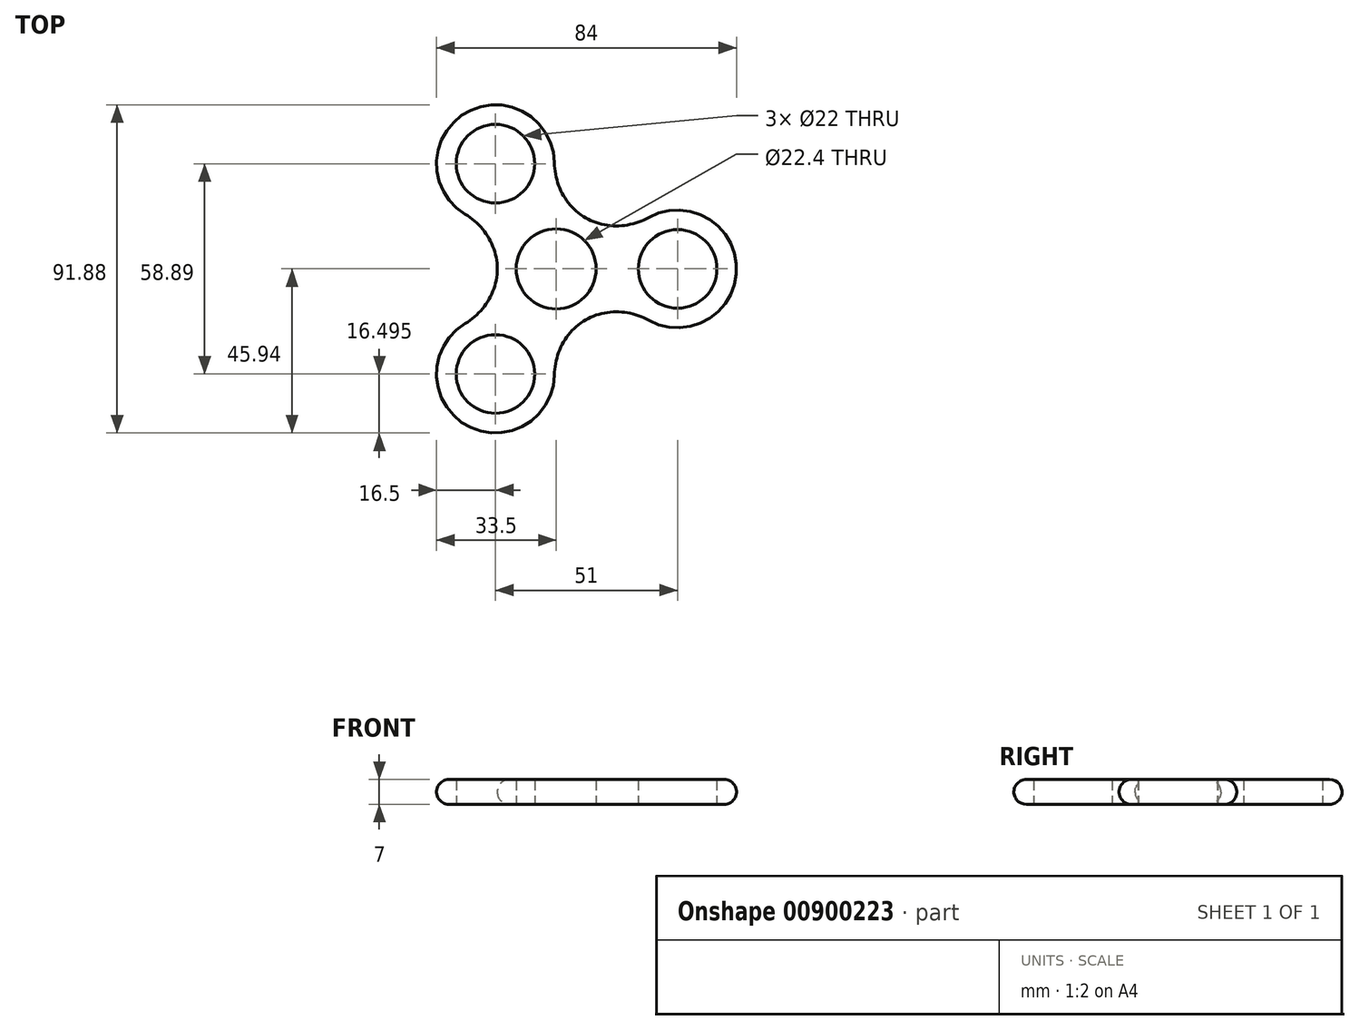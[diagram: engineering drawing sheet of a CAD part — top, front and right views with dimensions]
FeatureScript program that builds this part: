
annotation { "Feature Type Name" : "Feature", "Feature Type Description" : "" }
export const myFeature = defineFeature(function(context is Context, id is Id, definition is map)
    precondition{}
    {
        {
            assignVariable(context, id + "F0", {"name" : "thick", "anyValue" : 7});
        }
        {
            var Q0;
            Q0=qCreatedBy(makeId("Top.planeOp"),FACE);
            var sketch = newSketch(context, id + "F1", { "sketchPlane" : qUnion([Q0])});
            skCircle(sketch, "E0", {"center": v(0, 0) * mm, "radius": 11.2 * mm});
            skCircle(sketch, "E1", {"center": v(0, 0) * mm, "radius": 16.5 * mm});
            skCircle(sketch, "E2.1.0.0", {"center": v(34, 0) * mm, "radius": 16.5 * mm});
            skCircle(sketch, "E2.1.0.1", {"center": v(34, 0) * mm, "radius": 11 * mm});
            skLineSegment(sketch, "E2.direction2", {"start": v(0, 0) * mm, "end": v(0, 34) * mm, "construction": true});
            skCircle(sketch, "E3.1.0", {"center": v(-17, 29.44) * mm, "radius": 16.5 * mm});
            skCircle(sketch, "E3.1.1", {"center": v(-17, 29.44) * mm, "radius": 11 * mm});
            skCircle(sketch, "E3.2.0", {"center": v(-17, -29.44) * mm, "radius": 16.5 * mm});
            skCircle(sketch, "E3.2.1", {"center": v(-17, -29.44) * mm, "radius": 11 * mm});
            skLineSegment(sketch, "E4", {"start": v(0, 0) * mm, "end": v(-16.5, 0) * mm, "construction": true});
            skLineSegment(sketch, "E5.1.0", {"start": v(0, 0) * mm, "end": v(8.25, -14.29) * mm, "construction": true});
            skLineSegment(sketch, "E5.2.0", {"start": v(0, 0) * mm, "end": v(8.25, 14.29) * mm, "construction": true});
            skLineSegment(sketch, "E6", {"start": v(0, 0) * mm, "end": v(26, 14.43) * mm, "construction": true});
            skLineSegment(sketch, "E7.1.0", {"start": v(0, 0) * mm, "end": v(-25.5, 15.3) * mm, "construction": true});
            skLineSegment(sketch, "E7.2.0", {"start": v(0, 0) * mm, "end": v(-0.5, -29.72) * mm, "construction": true});
            skLineSegment(sketch, "E8", {"start": v(0, 0) * mm, "end": v(26, -14.43) * mm, "construction": true});
            skLineSegment(sketch, "E9.1.0", {"start": v(0, 0) * mm, "end": v(-0.5, 29.72) * mm, "construction": true});
            skLineSegment(sketch, "E9.2.0", {"start": v(0, 0) * mm, "end": v(-25.5, -15.3) * mm, "construction": true});
            skCircle(sketch, "E10", {"center": v(0, 0) * mm, "radius": 23 * mm, "construction": true});
            skFitSpline(sketch, "E11", {"points": [v(-0.5, 29.72) * mm, v(8.25, 14.29) * mm, v(26, 14.43) * mm], "startDerivative": vector(0.68, -40.36) * mm, "endDerivative": vector(35.3, 19.6) * mm});
            skFitSpline(sketch, "E12", {"points": [v(26, -14.43) * mm, v(8.25, -14.29) * mm, v(-0.5, -29.72) * mm], "startDerivative": vector(-35.3, 19.6) * mm, "endDerivative": vector(-0.68, -40.36) * mm});
            skFitSpline(sketch, "E13", {"points": [v(-25.5, -15.3) * mm, v(-16.5, 0) * mm, v(-25.5, 15.3) * mm], "startDerivative": vector(34.61, 20.77) * mm, "endDerivative": vector(-34.61, 20.77) * mm});
            skSolve(sketch);
        }
        {
            var Q0;
            Q0=makeQuery(id+"F1.imprint","IMPRINT",FACE,{"disambiguationData":[TD([[makeQuery(id+"F1.imprint","IMPRINT",EDGE,{"derivedFrom":sQuery(id+"F1.wireOp",EDGE,"E3.1.1")}),-1.0]])]});
            var Q1;
            Q1=makeQuery(id+"F1.imprint","IMPRINT",FACE,{"disambiguationData":[TD([[makeQuery(id+"F1.imprint","IMPRINT",EDGE,{"derivedFrom":sQuery(id+"F1.wireOp",EDGE,"E2.1.0.1")}),-1.0]])]});
            var Q2;
            Q2=makeQuery(id+"F1.imprint","IMPRINT",FACE,{"disambiguationData":[TD([[makeQuery(id+"F1.imprint","IMPRINT",EDGE,{"derivedFrom":sQuery(id+"F1.wireOp",EDGE,"E3.2.1")}),-1.0]])]});
            var Q3;
            {var subQ0=sQuery(id+"F1.wireOp",EDGE,"0fb8827f-fbdd-4e70-864b-5845bb5293e8.2.1");var subQ1=sQuery(id+"F1.wireOp",EDGE,"E1");var subQ2=makeQuery(id+"F1.imprint","INTERSECT",VERTEX,{"derivedFrom":[subQ1,subQ0]});Q3=makeQuery(id+"F1.imprint","IMPRINT",FACE,{"disambiguationData":[TD([[makeQuery(id+"F1.imprint","IMPRINT",EDGE,{"disambiguationData":[TD([[subQ2,-1.0]])],"derivedFrom":subQ1}),-1.0]])]});}
            var Q4;
            {var subQ1=sQuery(id+"F1.wireOp",EDGE,"E1");var subQ3=sQuery(id+"F1.wireOp",EDGE,"0fb8827f-fbdd-4e70-864b-5845bb5293e8.2.1");var subQ4=makeQuery(id+"F1.imprint","INTERSECT",VERTEX,{"derivedFrom":[subQ1,subQ3]});Q4=makeQuery(id+"F1.imprint","IMPRINT",FACE,{"disambiguationData":[TD([[makeQuery(id+"F1.imprint","IMPRINT",EDGE,{"disambiguationData":[TD([[subQ4,1.0]])],"derivedFrom":subQ1}),-1.0]])]});}
            var Q5;
            {var subQ1=sQuery(id+"F1.wireOp",EDGE,"E1");var subQ3=sQuery(id+"F1.wireOp",EDGE,"0fb8827f-fbdd-4e70-864b-5845bb5293e8.2.0");var subQ4=makeQuery(id+"F1.imprint","INTERSECT",VERTEX,{"derivedFrom":[subQ1,subQ3]});Q5=makeQuery(id+"F1.imprint","IMPRINT",FACE,{"disambiguationData":[TD([[makeQuery(id+"F1.imprint","IMPRINT",EDGE,{"disambiguationData":[TD([[subQ4,-1.0]])],"derivedFrom":subQ1}),-1.0]])]});}
            var Q6;
            {var subQ1=sQuery(id+"F1.wireOp",EDGE,"E1");var subQ3=sQuery(id+"F1.wireOp",EDGE,"AmyeHJv8-f6Uf-TbtG-oV3R-gP925QMOtAnL");var subQ4=makeQuery(id+"F1.imprint","INTERSECT",VERTEX,{"derivedFrom":[subQ1,subQ3]});Q6=makeQuery(id+"F1.imprint","IMPRINT",FACE,{"disambiguationData":[TD([[makeQuery(id+"F1.imprint","IMPRINT",EDGE,{"disambiguationData":[TD([[subQ4,1.0]])],"derivedFrom":subQ1}),-1.0]])]});}
            var Q7;
            {var subQ1=sQuery(id+"F1.wireOp",EDGE,"E1");var subQ3=sQuery(id+"F1.wireOp",EDGE,"KYfTjFGJ-pQUi-AP5x-4Sv7-9pKaKbr0BPRH");var subQ4=makeQuery(id+"F1.imprint","INTERSECT",VERTEX,{"derivedFrom":[subQ1,subQ3]});Q7=makeQuery(id+"F1.imprint","IMPRINT",FACE,{"disambiguationData":[TD([[makeQuery(id+"F1.imprint","IMPRINT",EDGE,{"disambiguationData":[TD([[subQ4,-1.0]])],"derivedFrom":subQ1}),-1.0]])]});}
            var Q8;
            {var subQ0=sQuery(id+"F1.wireOp",EDGE,"KYfTjFGJ-pQUi-AP5x-4Sv7-9pKaKbr0BPRH");var subQ1=sQuery(id+"F1.wireOp",EDGE,"E1");var subQ2=makeQuery(id+"F1.imprint","INTERSECT",VERTEX,{"derivedFrom":[subQ1,subQ0]});Q8=makeQuery(id+"F1.imprint","IMPRINT",FACE,{"disambiguationData":[TD([[makeQuery(id+"F1.imprint","IMPRINT",EDGE,{"disambiguationData":[TD([[subQ2,1.0]])],"derivedFrom":subQ1}),-1.0]])]});}
            var Q9;
            {var subQ0=sQuery(id+"F1.wireOp",EDGE,"0fb8827f-fbdd-4e70-864b-5845bb5293e8.1.1");var subQ1=sQuery(id+"F1.wireOp",EDGE,"E1");var subQ2=makeQuery(id+"F1.imprint","INTERSECT",VERTEX,{"derivedFrom":[subQ1,subQ0]});Q9=makeQuery(id+"F1.imprint","IMPRINT",FACE,{"disambiguationData":[TD([[makeQuery(id+"F1.imprint","IMPRINT",EDGE,{"disambiguationData":[TD([[subQ2,-1.0]])],"derivedFrom":subQ1}),-1.0]])]});}
            var Q10;
            {var subQ1=sQuery(id+"F1.wireOp",EDGE,"E1");var subQ3=sQuery(id+"F1.wireOp",EDGE,"0fb8827f-fbdd-4e70-864b-5845bb5293e8.1.1");var subQ4=makeQuery(id+"F1.imprint","INTERSECT",VERTEX,{"derivedFrom":[subQ1,subQ3]});Q10=makeQuery(id+"F1.imprint","IMPRINT",FACE,{"disambiguationData":[TD([[makeQuery(id+"F1.imprint","IMPRINT",EDGE,{"disambiguationData":[TD([[subQ4,1.0]])],"derivedFrom":subQ1}),-1.0]])]});}
            var Q11;
            {var subQ1=sQuery(id+"F1.wireOp",EDGE,"E1");var subQ3=sQuery(id+"F1.wireOp",EDGE,"0fb8827f-fbdd-4e70-864b-5845bb5293e8.1.0");var subQ4=makeQuery(id+"F1.imprint","INTERSECT",VERTEX,{"derivedFrom":[subQ1,subQ3]});Q11=makeQuery(id+"F1.imprint","IMPRINT",FACE,{"disambiguationData":[TD([[makeQuery(id+"F1.imprint","IMPRINT",EDGE,{"disambiguationData":[TD([[subQ4,-1.0]])],"derivedFrom":subQ1}),-1.0]])]});}
            var Q12;
            {var subQ0=sQuery(id+"F1.wireOp",EDGE,"0fb8827f-fbdd-4e70-864b-5845bb5293e8.1.0");var subQ1=sQuery(id+"F1.wireOp",EDGE,"E0");var subQ2=makeQuery(id+"F1.imprint","INTERSECT",VERTEX,{"derivedFrom":[subQ1,subQ0]});Q12=makeQuery(id+"F1.imprint","IMPRINT",FACE,{"disambiguationData":[TD([[makeQuery(id+"F1.imprint","IMPRINT",EDGE,{"disambiguationData":[TD([[subQ2,-1.0]])],"derivedFrom":subQ1}),-1.0]])]});}
            var Q13;
            {var subQ0=sQuery(id+"F1.wireOp",EDGE,"0fb8827f-fbdd-4e70-864b-5845bb5293e8.1.1");var subQ1=sQuery(id+"F1.wireOp",EDGE,"E0");var subQ2=makeQuery(id+"F1.imprint","INTERSECT",VERTEX,{"derivedFrom":[subQ1,subQ0]});Q13=makeQuery(id+"F1.imprint","IMPRINT",FACE,{"disambiguationData":[TD([[makeQuery(id+"F1.imprint","IMPRINT",EDGE,{"disambiguationData":[TD([[subQ2,-1.0]])],"derivedFrom":subQ1}),-1.0]])]});}
            var Q14;
            {var subQ0=sQuery(id+"F1.wireOp",EDGE,"11e8347d-43cd-4a78-95db-13a0e71d93fb.2.0");var subQ1=sQuery(id+"F1.wireOp",EDGE,"E0");var subQ2=makeQuery(id+"F1.imprint","INTERSECT",VERTEX,{"derivedFrom":[subQ1,subQ0]});Q14=makeQuery(id+"F1.imprint","IMPRINT",FACE,{"disambiguationData":[TD([[makeQuery(id+"F1.imprint","IMPRINT",EDGE,{"disambiguationData":[TD([[subQ2,-1.0]])],"derivedFrom":subQ1}),-1.0]])]});}
            var Q15;
            {var subQ0=sQuery(id+"F1.wireOp",EDGE,"11e8347d-43cd-4a78-95db-13a0e71d93fb.2.0");var subQ1=sQuery(id+"F1.wireOp",EDGE,"E0");var subQ2=makeQuery(id+"F1.imprint","INTERSECT",VERTEX,{"derivedFrom":[subQ1,subQ0]});Q15=makeQuery(id+"F1.imprint","IMPRINT",FACE,{"disambiguationData":[TD([[makeQuery(id+"F1.imprint","IMPRINT",EDGE,{"disambiguationData":[TD([[subQ2,1.0]])],"derivedFrom":subQ1}),-1.0]])]});}
            var Q16;
            {var subQ0=sQuery(id+"F1.wireOp",EDGE,"KYfTjFGJ-pQUi-AP5x-4Sv7-9pKaKbr0BPRH");var subQ1=sQuery(id+"F1.wireOp",EDGE,"E0");var subQ2=makeQuery(id+"F1.imprint","INTERSECT",VERTEX,{"derivedFrom":[subQ1,subQ0]});Q16=makeQuery(id+"F1.imprint","IMPRINT",FACE,{"disambiguationData":[TD([[makeQuery(id+"F1.imprint","IMPRINT",EDGE,{"disambiguationData":[TD([[subQ2,1.0]])],"derivedFrom":subQ1}),-1.0]])]});}
            var Q17;
            {var subQ0=sQuery(id+"F1.wireOp",EDGE,"11e8347d-43cd-4a78-95db-13a0e71d93fb.1.0");var subQ1=sQuery(id+"F1.wireOp",EDGE,"E0");var subQ2=makeQuery(id+"F1.imprint","INTERSECT",VERTEX,{"derivedFrom":[subQ1,subQ0]});Q17=makeQuery(id+"F1.imprint","IMPRINT",FACE,{"disambiguationData":[TD([[makeQuery(id+"F1.imprint","IMPRINT",EDGE,{"disambiguationData":[TD([[subQ2,-1.0]])],"derivedFrom":subQ1}),-1.0]])]});}
            var Q18;
            {var subQ0=sQuery(id+"F1.wireOp",EDGE,"0fb8827f-fbdd-4e70-864b-5845bb5293e8.2.0");var subQ1=sQuery(id+"F1.wireOp",EDGE,"E0");var subQ2=makeQuery(id+"F1.imprint","INTERSECT",VERTEX,{"derivedFrom":[subQ1,subQ0]});Q18=makeQuery(id+"F1.imprint","IMPRINT",FACE,{"disambiguationData":[TD([[makeQuery(id+"F1.imprint","IMPRINT",EDGE,{"disambiguationData":[TD([[subQ2,-1.0]])],"derivedFrom":subQ1}),-1.0]])]});}
            var Q19;
            {var subQ0=sQuery(id+"F1.wireOp",EDGE,"0fb8827f-fbdd-4e70-864b-5845bb5293e8.2.1");var subQ1=sQuery(id+"F1.wireOp",EDGE,"E0");var subQ2=makeQuery(id+"F1.imprint","INTERSECT",VERTEX,{"derivedFrom":[subQ1,subQ0]});Q19=makeQuery(id+"F1.imprint","IMPRINT",FACE,{"disambiguationData":[TD([[makeQuery(id+"F1.imprint","IMPRINT",EDGE,{"disambiguationData":[TD([[subQ2,-1.0]])],"derivedFrom":subQ1}),-1.0]])]});}
            var Q20;
            {var subQ0=sQuery(id+"F1.wireOp",EDGE,"3LaCC265-mUxf-RXKi-feVW-1q0p3KE8BSpX");var subQ1=sQuery(id+"F1.wireOp",EDGE,"E0");var subQ2=makeQuery(id+"F1.imprint","INTERSECT",VERTEX,{"derivedFrom":[subQ1,subQ0]});Q20=makeQuery(id+"F1.imprint","IMPRINT",FACE,{"disambiguationData":[TD([[makeQuery(id+"F1.imprint","IMPRINT",EDGE,{"disambiguationData":[TD([[subQ2,-1.0]])],"derivedFrom":subQ1}),-1.0]])]});}
            var Q21;
            {var subQ1=sQuery(id+"F1.wireOp",EDGE,"E3.1.0");var subQ3=sQuery(id+"F1.wireOp",EDGE,"fSNLGB0O-ToKY-NnpY-kWFq-t0aRrDztOWBC");var subQ4=makeQuery(id+"F1.imprint","INTERSECT",VERTEX,{"derivedFrom":[subQ1,subQ3]});Q21=makeQuery(id+"F1.imprint","IMPRINT",FACE,{"disambiguationData":[TD([[makeQuery(id+"F1.imprint","IMPRINT",EDGE,{"disambiguationData":[TD([[subQ4,-1.0]])],"derivedFrom":subQ3}),-1.0]])]});}
            var Q22;
            {var subQ0=sQuery(id+"F1.wireOp",EDGE,"487b85fb-fa4c-4945-8efc-abb3d7273f0f");var subQ3=sQuery(id+"F1.wireOp",EDGE,"fSNLGB0O-ToKY-NnpY-kWFq-t0aRrDztOWBC");var subQ5=makeQuery(id+"F1.imprint","INTERSECT",VERTEX,{"disambiguationData":[OD(0.0)],"derivedFrom":[subQ3,subQ0]});Q22=makeQuery(id+"F1.imprint","IMPRINT",FACE,{"disambiguationData":[TD([[makeQuery(id+"F1.imprint","IMPRINT",EDGE,{"disambiguationData":[TD([[subQ5,1.0]])],"derivedFrom":subQ3}),-1.0]])]});}
            var Q23;
            {var subQ0=sQuery(id+"F1.wireOp",EDGE,"a5bf1b23-31b3-41ea-81d9-f0380b37c509");var subQ3=sQuery(id+"F1.wireOp",EDGE,"fSNLGB0O-ToKY-NnpY-kWFq-t0aRrDztOWBC");var subQ5=makeQuery(id+"F1.imprint","INTERSECT",VERTEX,{"disambiguationData":[OD(1.0)],"derivedFrom":[subQ3,subQ0]});Q23=makeQuery(id+"F1.imprint","IMPRINT",FACE,{"disambiguationData":[TD([[makeQuery(id+"F1.imprint","IMPRINT",EDGE,{"disambiguationData":[TD([[subQ5,-1.0]])],"derivedFrom":subQ3}),-1.0]])]});}
            var Q24;
            {var subQ1=sQuery(id+"F1.wireOp",EDGE,"E3.1.0");var subQ3=sQuery(id+"F1.wireOp",EDGE,"fSNLGB0O-ToKY-NnpY-kWFq-t0aRrDztOWBC");var subQ4=makeQuery(id+"F1.imprint","INTERSECT",VERTEX,{"derivedFrom":[subQ1,subQ3]});Q24=makeQuery(id+"F1.imprint","IMPRINT",FACE,{"disambiguationData":[TD([[makeQuery(id+"F1.imprint","IMPRINT",EDGE,{"disambiguationData":[TD([[subQ4,1.0]])],"derivedFrom":subQ3}),-1.0]])]});}
            var Q25;
            {var subQ1=sQuery(id+"F1.wireOp",EDGE,"E2.1.0.0");var subQ3=sQuery(id+"F1.wireOp",EDGE,"fSNLGB0O-ToKY-NnpY-kWFq-t0aRrDztOWBC");var subQ4=makeQuery(id+"F1.imprint","INTERSECT",VERTEX,{"derivedFrom":[subQ1,subQ3]});Q25=makeQuery(id+"F1.imprint","IMPRINT",FACE,{"disambiguationData":[TD([[makeQuery(id+"F1.imprint","IMPRINT",EDGE,{"disambiguationData":[TD([[subQ4,-1.0]])],"derivedFrom":subQ3}),-1.0]])]});}
            var Q26;
            {var subQ0=sQuery(id+"F1.wireOp",EDGE,"a5bf1b23-31b3-41ea-81d9-f0380b37c509");var subQ3=sQuery(id+"F1.wireOp",EDGE,"fSNLGB0O-ToKY-NnpY-kWFq-t0aRrDztOWBC");var subQ5=makeQuery(id+"F1.imprint","INTERSECT",VERTEX,{"disambiguationData":[OD(0.0)],"derivedFrom":[subQ3,subQ0]});Q26=makeQuery(id+"F1.imprint","IMPRINT",FACE,{"disambiguationData":[TD([[makeQuery(id+"F1.imprint","IMPRINT",EDGE,{"disambiguationData":[TD([[subQ5,1.0]])],"derivedFrom":subQ3}),-1.0]])]});}
            var Q27;
            {var subQ1=sQuery(id+"F1.wireOp",EDGE,"E2.1.0.0");var subQ3=sQuery(id+"F1.wireOp",EDGE,"fSNLGB0O-ToKY-NnpY-kWFq-t0aRrDztOWBC");var subQ4=makeQuery(id+"F1.imprint","INTERSECT",VERTEX,{"derivedFrom":[subQ1,subQ3]});Q27=makeQuery(id+"F1.imprint","IMPRINT",FACE,{"disambiguationData":[TD([[makeQuery(id+"F1.imprint","IMPRINT",EDGE,{"disambiguationData":[TD([[subQ4,1.0]])],"derivedFrom":subQ3}),-1.0]])]});}
            var Q28;
            {var subQ0=sQuery(id+"F1.wireOp",EDGE,"0ac61488-3549-4979-853d-932dcf3a4109");var subQ3=sQuery(id+"F1.wireOp",EDGE,"fSNLGB0O-ToKY-NnpY-kWFq-t0aRrDztOWBC");var subQ5=makeQuery(id+"F1.imprint","INTERSECT",VERTEX,{"disambiguationData":[OD(1.0)],"derivedFrom":[subQ3,subQ0]});Q28=makeQuery(id+"F1.imprint","IMPRINT",FACE,{"disambiguationData":[TD([[makeQuery(id+"F1.imprint","IMPRINT",EDGE,{"disambiguationData":[TD([[subQ5,-1.0]])],"derivedFrom":subQ3}),-1.0]])]});}
            var Q29;
            {var subQ1=sQuery(id+"F1.wireOp",EDGE,"E3.2.0");var subQ3=sQuery(id+"F1.wireOp",EDGE,"fSNLGB0O-ToKY-NnpY-kWFq-t0aRrDztOWBC");var subQ4=makeQuery(id+"F1.imprint","INTERSECT",VERTEX,{"derivedFrom":[subQ1,subQ3]});Q29=makeQuery(id+"F1.imprint","IMPRINT",FACE,{"disambiguationData":[TD([[makeQuery(id+"F1.imprint","IMPRINT",EDGE,{"disambiguationData":[TD([[subQ4,-1.0]])],"derivedFrom":subQ3}),-1.0]])]});}
            var Q30;
            {var subQ0=sQuery(id+"F1.wireOp",EDGE,"0ac61488-3549-4979-853d-932dcf3a4109");var subQ3=sQuery(id+"F1.wireOp",EDGE,"fSNLGB0O-ToKY-NnpY-kWFq-t0aRrDztOWBC");var subQ5=makeQuery(id+"F1.imprint","INTERSECT",VERTEX,{"disambiguationData":[OD(0.0)],"derivedFrom":[subQ3,subQ0]});Q30=makeQuery(id+"F1.imprint","IMPRINT",FACE,{"disambiguationData":[TD([[makeQuery(id+"F1.imprint","IMPRINT",EDGE,{"disambiguationData":[TD([[subQ5,1.0]])],"derivedFrom":subQ3}),-1.0]])]});}
            var Q31;
            {var subQ1=sQuery(id+"F1.wireOp",EDGE,"E3.2.0");var subQ3=sQuery(id+"F1.wireOp",EDGE,"fSNLGB0O-ToKY-NnpY-kWFq-t0aRrDztOWBC");var subQ4=makeQuery(id+"F1.imprint","INTERSECT",VERTEX,{"derivedFrom":[subQ1,subQ3]});Q31=makeQuery(id+"F1.imprint","IMPRINT",FACE,{"disambiguationData":[TD([[makeQuery(id+"F1.imprint","IMPRINT",EDGE,{"disambiguationData":[TD([[subQ4,1.0]])],"derivedFrom":subQ3}),-1.0]])]});}
            var Q32;
            {var subQ0=sQuery(id+"F1.wireOp",EDGE,"487b85fb-fa4c-4945-8efc-abb3d7273f0f");var subQ3=sQuery(id+"F1.wireOp",EDGE,"fSNLGB0O-ToKY-NnpY-kWFq-t0aRrDztOWBC");var subQ5=makeQuery(id+"F1.imprint","INTERSECT",VERTEX,{"disambiguationData":[OD(1.0)],"derivedFrom":[subQ3,subQ0]});Q32=makeQuery(id+"F1.imprint","IMPRINT",FACE,{"disambiguationData":[TD([[makeQuery(id+"F1.imprint","IMPRINT",EDGE,{"disambiguationData":[TD([[subQ5,-1.0]])],"derivedFrom":subQ3}),-1.0]])]});}
            extrude(context, id + "F2", {"entities" : qUnion([Q0, Q1, Q2, Q3, Q4, Q5, Q6, Q7, Q8, Q9, Q10, Q11, Q12, Q13, Q14, Q15, Q16, Q17, Q18, Q19, Q20, Q21, Q22, Q23, Q24, Q25, Q26, Q27, Q28, Q29, Q30, Q31, Q32]), "endBound" : BoundingType.SYMMETRIC, "depth" : getVariable(context, 'thick') * mm, "offsetDistance" : 25 * mm});
        }
        {
            var Q0;
            Q0=makeQuery(id+"F2.opExtrude","CAP_EDGE",EDGE,{"disambiguationData":[OSD([sQuery(id+"F1.wireOp",EDGE,"E3.2.0")])],"isStart":false});
            var Q1;
            Q1=makeQuery(id+"F2.opExtrude","CAP_EDGE",EDGE,{"disambiguationData":[OSD([sQuery(id+"F1.wireOp",EDGE,"E3.2.0")])],"isStart":true});
            fillet(context, id + "F3", {"entities" : qUnion([Q0, Q1]), "radius" : (getVariable(context, 'thick') / 2) * mm, "tangentPropagation" : true, "allowEdgeOverflow" : false});
        }
    });
